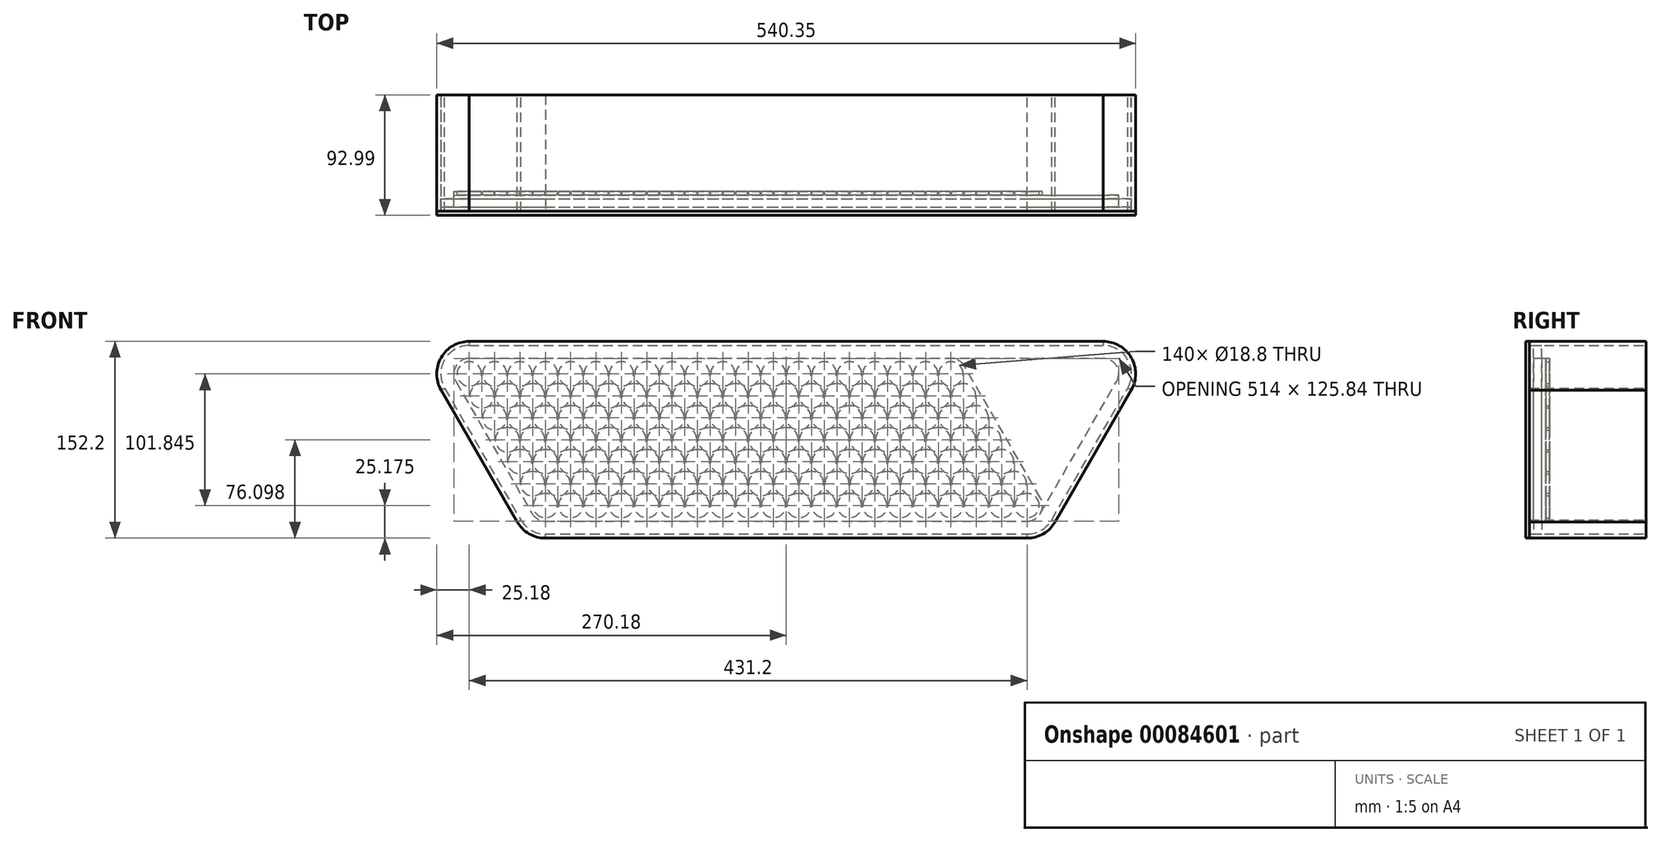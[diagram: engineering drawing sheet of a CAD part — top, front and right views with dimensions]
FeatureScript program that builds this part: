
annotation { "Feature Type Name" : "Feature", "Feature Type Description" : "" }
export const myFeature = defineFeature(function(context is Context, id is Id, definition is map)
    precondition{}
    {
        {
            var Q0;
            Q0=qCreatedBy(makeId("Front.planeOp"),FACE);
            var sketch = newSketch(context, id + "F0", { "sketchPlane" : qUnion([Q0]) });
            skLineSegment(sketch, "E0", {"start": v(0, 0) * mm, "end": v(79.44, 0) * mm, "construction": true});
            skLineSegment(sketch, "E1", {"start": v(0, 0) * mm, "end": v(43.4, -75.16) * mm, "construction": true});
            skCircle(sketch, "E2", {"center": v(0, 0) * mm, "radius": 9.4 * mm});
            skCircle(sketch, "E3.1.0.0", {"center": v(19.6, 0) * mm, "radius": 9.4 * mm});
            skCircle(sketch, "E3.2.0.0", {"center": v(39.2, 0) * mm, "radius": 9.4 * mm});
            skCircle(sketch, "E3.3.0.0", {"center": v(58.8, 0) * mm, "radius": 9.4 * mm});
            skCircle(sketch, "E3.4.0.0", {"center": v(78.4, 0) * mm, "radius": 9.4 * mm});
            skCircle(sketch, "E3.5.0.0", {"center": v(98, 0) * mm, "radius": 9.4 * mm});
            skCircle(sketch, "E3.6.0.0", {"center": v(117.6, 0) * mm, "radius": 9.4 * mm});
            skCircle(sketch, "E3.7.0.0", {"center": v(137.2, 0) * mm, "radius": 9.4 * mm});
            skCircle(sketch, "E3.8.0.0", {"center": v(156.8, 0) * mm, "radius": 9.4 * mm});
            skCircle(sketch, "E3.9.0.0", {"center": v(176.4, 0) * mm, "radius": 9.4 * mm});
            skCircle(sketch, "E3.10.0.0", {"center": v(196, 0) * mm, "radius": 9.4 * mm});
            skCircle(sketch, "E3.11.0.0", {"center": v(215.6, 0) * mm, "radius": 9.4 * mm});
            skCircle(sketch, "E3.12.0.0", {"center": v(235.2, 0) * mm, "radius": 9.4 * mm});
            skCircle(sketch, "E3.13.0.0", {"center": v(254.8, 0) * mm, "radius": 9.4 * mm});
            skCircle(sketch, "E3.14.0.0", {"center": v(274.4, 0) * mm, "radius": 9.4 * mm});
            skCircle(sketch, "E3.15.0.0", {"center": v(294, 0) * mm, "radius": 9.4 * mm});
            skCircle(sketch, "E3.16.0.0", {"center": v(313.6, 0) * mm, "radius": 9.4 * mm});
            skCircle(sketch, "E3.17.0.0", {"center": v(333.2, 0) * mm, "radius": 9.4 * mm});
            skCircle(sketch, "E3.18.0.0", {"center": v(352.8, 0) * mm, "radius": 9.4 * mm});
            skCircle(sketch, "E3.19.0.0", {"center": v(372.4, 0) * mm, "radius": 9.4 * mm});
            skLineSegment(sketch, "E3.direction1", {"start": v(0, 0) * mm, "end": v(19.6, 0) * mm, "construction": true});
            skCircle(sketch, "E4.1.0.0", {"center": v(9.8, -16.97) * mm, "radius": 9.4 * mm});
            skCircle(sketch, "E4.2.0.0", {"center": v(19.6, -33.95) * mm, "radius": 9.4 * mm});
            skCircle(sketch, "E4.3.0.0", {"center": v(29.4, -50.92) * mm, "radius": 9.4 * mm});
            skCircle(sketch, "E4.4.0.0", {"center": v(39.2, -67.9) * mm, "radius": 9.4 * mm});
            skCircle(sketch, "E4.5.0.0", {"center": v(49, -84.87) * mm, "radius": 9.4 * mm});
            skCircle(sketch, "E4.6.0.0", {"center": v(58.8, -101.84) * mm, "radius": 9.4 * mm});
            skLineSegment(sketch, "E4.direction1", {"start": v(0, 0) * mm, "end": v(9.8, -16.97) * mm, "construction": true});
            skCircle(sketch, "E5.1.0.0", {"center": v(29.4, -16.97) * mm, "radius": 9.4 * mm});
            skCircle(sketch, "E5.1.0.1", {"center": v(39.2, -33.95) * mm, "radius": 9.4 * mm});
            skCircle(sketch, "E5.1.0.2", {"center": v(49, -50.92) * mm, "radius": 9.4 * mm});
            skCircle(sketch, "E5.1.0.3", {"center": v(58.8, -67.9) * mm, "radius": 9.4 * mm});
            skCircle(sketch, "E5.1.0.4", {"center": v(68.6, -84.87) * mm, "radius": 9.4 * mm});
            skCircle(sketch, "E5.1.0.5", {"center": v(78.4, -101.84) * mm, "radius": 9.4 * mm});
            skCircle(sketch, "E5.2.0.0", {"center": v(49, -16.97) * mm, "radius": 9.4 * mm});
            skCircle(sketch, "E5.2.0.1", {"center": v(58.8, -33.95) * mm, "radius": 9.4 * mm});
            skCircle(sketch, "E5.2.0.2", {"center": v(68.6, -50.92) * mm, "radius": 9.4 * mm});
            skCircle(sketch, "E5.2.0.3", {"center": v(78.4, -67.9) * mm, "radius": 9.4 * mm});
            skCircle(sketch, "E5.2.0.4", {"center": v(88.2, -84.87) * mm, "radius": 9.4 * mm});
            skCircle(sketch, "E5.2.0.5", {"center": v(98, -101.84) * mm, "radius": 9.4 * mm});
            skCircle(sketch, "E5.3.0.0", {"center": v(68.6, -16.97) * mm, "radius": 9.4 * mm});
            skCircle(sketch, "E5.3.0.1", {"center": v(78.4, -33.95) * mm, "radius": 9.4 * mm});
            skCircle(sketch, "E5.3.0.2", {"center": v(88.2, -50.92) * mm, "radius": 9.4 * mm});
            skCircle(sketch, "E5.3.0.3", {"center": v(98, -67.9) * mm, "radius": 9.4 * mm});
            skCircle(sketch, "E5.3.0.4", {"center": v(107.8, -84.87) * mm, "radius": 9.4 * mm});
            skCircle(sketch, "E5.3.0.5", {"center": v(117.6, -101.84) * mm, "radius": 9.4 * mm});
            skCircle(sketch, "E5.4.0.0", {"center": v(88.2, -16.97) * mm, "radius": 9.4 * mm});
            skCircle(sketch, "E5.4.0.1", {"center": v(98, -33.95) * mm, "radius": 9.4 * mm});
            skCircle(sketch, "E5.4.0.2", {"center": v(107.8, -50.92) * mm, "radius": 9.4 * mm});
            skCircle(sketch, "E5.4.0.3", {"center": v(117.6, -67.9) * mm, "radius": 9.4 * mm});
            skCircle(sketch, "E5.4.0.4", {"center": v(127.4, -84.87) * mm, "radius": 9.4 * mm});
            skCircle(sketch, "E5.4.0.5", {"center": v(137.2, -101.84) * mm, "radius": 9.4 * mm});
            skCircle(sketch, "E5.5.0.0", {"center": v(107.8, -16.97) * mm, "radius": 9.4 * mm});
            skCircle(sketch, "E5.5.0.1", {"center": v(117.6, -33.95) * mm, "radius": 9.4 * mm});
            skCircle(sketch, "E5.5.0.2", {"center": v(127.4, -50.92) * mm, "radius": 9.4 * mm});
            skCircle(sketch, "E5.5.0.3", {"center": v(137.2, -67.9) * mm, "radius": 9.4 * mm});
            skCircle(sketch, "E5.5.0.4", {"center": v(147, -84.87) * mm, "radius": 9.4 * mm});
            skCircle(sketch, "E5.5.0.5", {"center": v(156.8, -101.84) * mm, "radius": 9.4 * mm});
            skCircle(sketch, "E5.6.0.0", {"center": v(127.4, -16.97) * mm, "radius": 9.4 * mm});
            skCircle(sketch, "E5.6.0.1", {"center": v(137.2, -33.95) * mm, "radius": 9.4 * mm});
            skCircle(sketch, "E5.6.0.2", {"center": v(147, -50.92) * mm, "radius": 9.4 * mm});
            skCircle(sketch, "E5.6.0.3", {"center": v(156.8, -67.9) * mm, "radius": 9.4 * mm});
            skCircle(sketch, "E5.6.0.4", {"center": v(166.6, -84.87) * mm, "radius": 9.4 * mm});
            skCircle(sketch, "E5.6.0.5", {"center": v(176.4, -101.84) * mm, "radius": 9.4 * mm});
            skCircle(sketch, "E5.7.0.0", {"center": v(147, -16.97) * mm, "radius": 9.4 * mm});
            skCircle(sketch, "E5.7.0.1", {"center": v(156.8, -33.95) * mm, "radius": 9.4 * mm});
            skCircle(sketch, "E5.7.0.2", {"center": v(166.6, -50.92) * mm, "radius": 9.4 * mm});
            skCircle(sketch, "E5.7.0.3", {"center": v(176.4, -67.9) * mm, "radius": 9.4 * mm});
            skCircle(sketch, "E5.7.0.4", {"center": v(186.2, -84.87) * mm, "radius": 9.4 * mm});
            skCircle(sketch, "E5.7.0.5", {"center": v(196, -101.84) * mm, "radius": 9.4 * mm});
            skCircle(sketch, "E5.8.0.0", {"center": v(166.6, -16.97) * mm, "radius": 9.4 * mm});
            skCircle(sketch, "E5.8.0.1", {"center": v(176.4, -33.95) * mm, "radius": 9.4 * mm});
            skCircle(sketch, "E5.8.0.2", {"center": v(186.2, -50.92) * mm, "radius": 9.4 * mm});
            skCircle(sketch, "E5.8.0.3", {"center": v(196, -67.9) * mm, "radius": 9.4 * mm});
            skCircle(sketch, "E5.8.0.4", {"center": v(205.8, -84.87) * mm, "radius": 9.4 * mm});
            skCircle(sketch, "E5.8.0.5", {"center": v(215.6, -101.84) * mm, "radius": 9.4 * mm});
            skCircle(sketch, "E5.9.0.0", {"center": v(186.2, -16.97) * mm, "radius": 9.4 * mm});
            skCircle(sketch, "E5.9.0.1", {"center": v(196, -33.95) * mm, "radius": 9.4 * mm});
            skCircle(sketch, "E5.9.0.2", {"center": v(205.8, -50.92) * mm, "radius": 9.4 * mm});
            skCircle(sketch, "E5.9.0.3", {"center": v(215.6, -67.9) * mm, "radius": 9.4 * mm});
            skCircle(sketch, "E5.9.0.4", {"center": v(225.4, -84.87) * mm, "radius": 9.4 * mm});
            skCircle(sketch, "E5.9.0.5", {"center": v(235.2, -101.84) * mm, "radius": 9.4 * mm});
            skCircle(sketch, "E5.10.0.0", {"center": v(205.8, -16.97) * mm, "radius": 9.4 * mm});
            skCircle(sketch, "E5.10.0.1", {"center": v(215.6, -33.95) * mm, "radius": 9.4 * mm});
            skCircle(sketch, "E5.10.0.2", {"center": v(225.4, -50.92) * mm, "radius": 9.4 * mm});
            skCircle(sketch, "E5.10.0.3", {"center": v(235.2, -67.9) * mm, "radius": 9.4 * mm});
            skCircle(sketch, "E5.10.0.4", {"center": v(245, -84.87) * mm, "radius": 9.4 * mm});
            skCircle(sketch, "E5.10.0.5", {"center": v(254.8, -101.84) * mm, "radius": 9.4 * mm});
            skCircle(sketch, "E5.11.0.0", {"center": v(225.4, -16.97) * mm, "radius": 9.4 * mm});
            skCircle(sketch, "E5.11.0.1", {"center": v(235.2, -33.95) * mm, "radius": 9.4 * mm});
            skCircle(sketch, "E5.11.0.2", {"center": v(245, -50.92) * mm, "radius": 9.4 * mm});
            skCircle(sketch, "E5.11.0.3", {"center": v(254.8, -67.9) * mm, "radius": 9.4 * mm});
            skCircle(sketch, "E5.11.0.4", {"center": v(264.6, -84.87) * mm, "radius": 9.4 * mm});
            skCircle(sketch, "E5.11.0.5", {"center": v(274.4, -101.84) * mm, "radius": 9.4 * mm});
            skCircle(sketch, "E5.12.0.0", {"center": v(245, -16.97) * mm, "radius": 9.4 * mm});
            skCircle(sketch, "E5.12.0.1", {"center": v(254.8, -33.95) * mm, "radius": 9.4 * mm});
            skCircle(sketch, "E5.12.0.2", {"center": v(264.6, -50.92) * mm, "radius": 9.4 * mm});
            skCircle(sketch, "E5.12.0.3", {"center": v(274.4, -67.9) * mm, "radius": 9.4 * mm});
            skCircle(sketch, "E5.12.0.4", {"center": v(284.2, -84.87) * mm, "radius": 9.4 * mm});
            skCircle(sketch, "E5.12.0.5", {"center": v(294, -101.84) * mm, "radius": 9.4 * mm});
            skCircle(sketch, "E5.13.0.0", {"center": v(264.6, -16.97) * mm, "radius": 9.4 * mm});
            skCircle(sketch, "E5.13.0.1", {"center": v(274.4, -33.95) * mm, "radius": 9.4 * mm});
            skCircle(sketch, "E5.13.0.2", {"center": v(284.2, -50.92) * mm, "radius": 9.4 * mm});
            skCircle(sketch, "E5.13.0.3", {"center": v(294, -67.9) * mm, "radius": 9.4 * mm});
            skCircle(sketch, "E5.13.0.4", {"center": v(303.8, -84.87) * mm, "radius": 9.4 * mm});
            skCircle(sketch, "E5.13.0.5", {"center": v(313.6, -101.84) * mm, "radius": 9.4 * mm});
            skCircle(sketch, "E5.14.0.0", {"center": v(284.2, -16.97) * mm, "radius": 9.4 * mm});
            skCircle(sketch, "E5.14.0.1", {"center": v(294, -33.95) * mm, "radius": 9.4 * mm});
            skCircle(sketch, "E5.14.0.2", {"center": v(303.8, -50.92) * mm, "radius": 9.4 * mm});
            skCircle(sketch, "E5.14.0.3", {"center": v(313.6, -67.9) * mm, "radius": 9.4 * mm});
            skCircle(sketch, "E5.14.0.4", {"center": v(323.4, -84.87) * mm, "radius": 9.4 * mm});
            skCircle(sketch, "E5.14.0.5", {"center": v(333.2, -101.84) * mm, "radius": 9.4 * mm});
            skCircle(sketch, "E5.15.0.0", {"center": v(303.8, -16.97) * mm, "radius": 9.4 * mm});
            skCircle(sketch, "E5.15.0.1", {"center": v(313.6, -33.95) * mm, "radius": 9.4 * mm});
            skCircle(sketch, "E5.15.0.2", {"center": v(323.4, -50.92) * mm, "radius": 9.4 * mm});
            skCircle(sketch, "E5.15.0.3", {"center": v(333.2, -67.9) * mm, "radius": 9.4 * mm});
            skCircle(sketch, "E5.15.0.4", {"center": v(343, -84.87) * mm, "radius": 9.4 * mm});
            skCircle(sketch, "E5.15.0.5", {"center": v(352.8, -101.84) * mm, "radius": 9.4 * mm});
            skCircle(sketch, "E5.16.0.0", {"center": v(323.4, -16.97) * mm, "radius": 9.4 * mm});
            skCircle(sketch, "E5.16.0.1", {"center": v(333.2, -33.95) * mm, "radius": 9.4 * mm});
            skCircle(sketch, "E5.16.0.2", {"center": v(343, -50.92) * mm, "radius": 9.4 * mm});
            skCircle(sketch, "E5.16.0.3", {"center": v(352.8, -67.9) * mm, "radius": 9.4 * mm});
            skCircle(sketch, "E5.16.0.4", {"center": v(362.6, -84.87) * mm, "radius": 9.4 * mm});
            skCircle(sketch, "E5.16.0.5", {"center": v(372.4, -101.84) * mm, "radius": 9.4 * mm});
            skCircle(sketch, "E5.17.0.0", {"center": v(343, -16.97) * mm, "radius": 9.4 * mm});
            skCircle(sketch, "E5.17.0.1", {"center": v(352.8, -33.95) * mm, "radius": 9.4 * mm});
            skCircle(sketch, "E5.17.0.2", {"center": v(362.6, -50.92) * mm, "radius": 9.4 * mm});
            skCircle(sketch, "E5.17.0.3", {"center": v(372.4, -67.9) * mm, "radius": 9.4 * mm});
            skCircle(sketch, "E5.17.0.4", {"center": v(382.2, -84.87) * mm, "radius": 9.4 * mm});
            skCircle(sketch, "E5.17.0.5", {"center": v(392, -101.84) * mm, "radius": 9.4 * mm});
            skCircle(sketch, "E5.18.0.0", {"center": v(362.6, -16.97) * mm, "radius": 9.4 * mm});
            skCircle(sketch, "E5.18.0.1", {"center": v(372.4, -33.95) * mm, "radius": 9.4 * mm});
            skCircle(sketch, "E5.18.0.2", {"center": v(382.2, -50.92) * mm, "radius": 9.4 * mm});
            skCircle(sketch, "E5.18.0.3", {"center": v(392, -67.9) * mm, "radius": 9.4 * mm});
            skCircle(sketch, "E5.18.0.4", {"center": v(401.8, -84.87) * mm, "radius": 9.4 * mm});
            skCircle(sketch, "E5.18.0.5", {"center": v(411.6, -101.84) * mm, "radius": 9.4 * mm});
            skCircle(sketch, "E5.19.0.0", {"center": v(382.2, -16.97) * mm, "radius": 9.4 * mm});
            skCircle(sketch, "E5.19.0.1", {"center": v(392, -33.95) * mm, "radius": 9.4 * mm});
            skCircle(sketch, "E5.19.0.2", {"center": v(401.8, -50.92) * mm, "radius": 9.4 * mm});
            skCircle(sketch, "E5.19.0.3", {"center": v(411.6, -67.9) * mm, "radius": 9.4 * mm});
            skCircle(sketch, "E5.19.0.4", {"center": v(421.4, -84.87) * mm, "radius": 9.4 * mm});
            skCircle(sketch, "E5.19.0.5", {"center": v(431.2, -101.84) * mm, "radius": 9.4 * mm});
            skLineSegment(sketch, "E5.direction1", {"start": v(9.8, -16.97) * mm, "end": v(29.4, -16.97) * mm, "construction": true});
            skLineSegment(sketch, "E6", {"start": v(0, 0) * mm, "end": v(372.4, 0) * mm, "construction": true});
            skLineSegment(sketch, "E7", {"start": v(372.4, 0) * mm, "end": v(441, -118.82) * mm, "construction": true});
            skLineSegment(sketch, "E8", {"start": v(441, -118.82) * mm, "end": v(68.6, -118.82) * mm, "construction": true});
            skLineSegment(sketch, "E9", {"start": v(68.6, -118.82) * mm, "end": v(0, 0) * mm, "construction": true});
            skArc(sketch, "E10", {"start": v(48.4, -107.84) * mm, "mid": v(52.8, -112.24) * mm, "end": v(58.8, -113.84) * mm});
            skArc(sketch, "E11", {"start": v(431.2, -113.84) * mm, "mid": v(441.6, -107.84) * mm, "end": v(441.6, -95.84) * mm});
            skArc(sketch, "E12", {"start": v(382.8, 6) * mm, "mid": v(378.4, 10.4) * mm, "end": v(372.4, 12) * mm});
            skArc(sketch, "E13", {"start": v(0, 12) * mm, "mid": v(-10.4, 6) * mm, "end": v(-10.4, -6) * mm});
            skLineSegment(sketch, "E14", {"start": v(0, 12) * mm, "end": v(372.4, 12) * mm});
            skLineSegment(sketch, "E15", {"start": v(-10.4, -6) * mm, "end": v(48.4, -107.84) * mm});
            skLineSegment(sketch, "E16", {"start": v(58.8, -113.84) * mm, "end": v(431.2, -113.84) * mm});
            skLineSegment(sketch, "E17", {"start": v(441.6, -95.84) * mm, "end": v(382.8, 6) * mm});
            skLineSegment(sketch, "E18", {"start": v(441.6, -107.84) * mm, "end": v(500.4, -6) * mm, "construction": true});
            skLineSegment(sketch, "E19", {"start": v(372.4, 12) * mm, "end": v(490, 12) * mm, "construction": true});
            skPoint(sketch, "E20.visualSharp", {"position": v(510.78, 12) * mm});
            skArc(sketch, "E20.filletArc", {"start": v(500.4, -6) * mm, "mid": v(500.4, 6) * mm, "end": v(490, 12) * mm, "construction": true});
            skSolve(sketch);
        }
        {
            var Q0;
            Q0=makeQuery(id+"F0.imprint","IMPRINT",FACE,{"disambiguationData":[TD([[makeQuery(id+"F0.imprint","IMPRINT",EDGE,{"derivedFrom":sQuery(id+"F0.wireOp",EDGE,"E2")}),-1.0]])]});
            extrude(context, id + "F1", {"entities" : qUnion([Q0]), "depth" : 3 * mm});
        }
        {
            var Q0;
            Q0=makeQuery(id+"F1.opExtrude","CAP_FACE",FACE,{"disambiguationData":[OSD([sQuery(id+"F0.wireOp",EDGE,"E2"),sQuery(id+"F0.wireOp",EDGE,"E3.1.0.0"),sQuery(id+"F0.wireOp",EDGE,"E3.2.0.0"),sQuery(id+"F0.wireOp",EDGE,"E3.3.0.0"),sQuery(id+"F0.wireOp",EDGE,"E3.4.0.0"),sQuery(id+"F0.wireOp",EDGE,"E3.5.0.0"),sQuery(id+"F0.wireOp",EDGE,"E3.6.0.0"),sQuery(id+"F0.wireOp",EDGE,"E3.7.0.0"),sQuery(id+"F0.wireOp",EDGE,"E3.8.0.0"),sQuery(id+"F0.wireOp",EDGE,"E3.9.0.0"),sQuery(id+"F0.wireOp",EDGE,"E3.10.0.0"),sQuery(id+"F0.wireOp",EDGE,"E3.11.0.0"),sQuery(id+"F0.wireOp",EDGE,"E3.12.0.0"),sQuery(id+"F0.wireOp",EDGE,"E3.13.0.0"),sQuery(id+"F0.wireOp",EDGE,"E3.14.0.0"),sQuery(id+"F0.wireOp",EDGE,"E3.15.0.0"),sQuery(id+"F0.wireOp",EDGE,"E3.16.0.0"),sQuery(id+"F0.wireOp",EDGE,"E3.17.0.0"),sQuery(id+"F0.wireOp",EDGE,"E3.18.0.0"),sQuery(id+"F0.wireOp",EDGE,"E3.19.0.0"),sQuery(id+"F0.wireOp",EDGE,"E4.1.0.0"),sQuery(id+"F0.wireOp",EDGE,"E4.2.0.0"),sQuery(id+"F0.wireOp",EDGE,"E4.3.0.0"),sQuery(id+"F0.wireOp",EDGE,"E4.4.0.0"),sQuery(id+"F0.wireOp",EDGE,"E4.5.0.0"),sQuery(id+"F0.wireOp",EDGE,"E4.6.0.0"),sQuery(id+"F0.wireOp",EDGE,"E5.1.0.0"),sQuery(id+"F0.wireOp",EDGE,"E5.1.0.1"),sQuery(id+"F0.wireOp",EDGE,"E5.1.0.2"),sQuery(id+"F0.wireOp",EDGE,"E5.1.0.3"),sQuery(id+"F0.wireOp",EDGE,"E5.1.0.4"),sQuery(id+"F0.wireOp",EDGE,"E5.1.0.5"),sQuery(id+"F0.wireOp",EDGE,"E5.2.0.0"),sQuery(id+"F0.wireOp",EDGE,"E5.2.0.1"),sQuery(id+"F0.wireOp",EDGE,"E5.2.0.2"),sQuery(id+"F0.wireOp",EDGE,"E5.2.0.3"),sQuery(id+"F0.wireOp",EDGE,"E5.2.0.4"),sQuery(id+"F0.wireOp",EDGE,"E5.2.0.5"),sQuery(id+"F0.wireOp",EDGE,"E5.3.0.0"),sQuery(id+"F0.wireOp",EDGE,"E5.3.0.1"),sQuery(id+"F0.wireOp",EDGE,"E5.3.0.2"),sQuery(id+"F0.wireOp",EDGE,"E5.3.0.3"),sQuery(id+"F0.wireOp",EDGE,"E5.3.0.4"),sQuery(id+"F0.wireOp",EDGE,"E5.3.0.5"),sQuery(id+"F0.wireOp",EDGE,"E5.4.0.0"),sQuery(id+"F0.wireOp",EDGE,"E5.4.0.1"),sQuery(id+"F0.wireOp",EDGE,"E5.4.0.2"),sQuery(id+"F0.wireOp",EDGE,"E5.4.0.3"),sQuery(id+"F0.wireOp",EDGE,"E5.4.0.4"),sQuery(id+"F0.wireOp",EDGE,"E5.4.0.5"),sQuery(id+"F0.wireOp",EDGE,"E5.5.0.0"),sQuery(id+"F0.wireOp",EDGE,"E5.5.0.1"),sQuery(id+"F0.wireOp",EDGE,"E5.5.0.2"),sQuery(id+"F0.wireOp",EDGE,"E5.5.0.3"),sQuery(id+"F0.wireOp",EDGE,"E5.5.0.4"),sQuery(id+"F0.wireOp",EDGE,"E5.5.0.5"),sQuery(id+"F0.wireOp",EDGE,"E5.6.0.0"),sQuery(id+"F0.wireOp",EDGE,"E5.6.0.1"),sQuery(id+"F0.wireOp",EDGE,"E5.6.0.2"),sQuery(id+"F0.wireOp",EDGE,"E5.6.0.3"),sQuery(id+"F0.wireOp",EDGE,"E5.6.0.4"),sQuery(id+"F0.wireOp",EDGE,"E5.6.0.5"),sQuery(id+"F0.wireOp",EDGE,"E5.7.0.0"),sQuery(id+"F0.wireOp",EDGE,"E5.7.0.1"),sQuery(id+"F0.wireOp",EDGE,"E5.7.0.2"),sQuery(id+"F0.wireOp",EDGE,"E5.7.0.3"),sQuery(id+"F0.wireOp",EDGE,"E5.7.0.4"),sQuery(id+"F0.wireOp",EDGE,"E5.7.0.5"),sQuery(id+"F0.wireOp",EDGE,"E5.8.0.0"),sQuery(id+"F0.wireOp",EDGE,"E5.8.0.1"),sQuery(id+"F0.wireOp",EDGE,"E5.8.0.2"),sQuery(id+"F0.wireOp",EDGE,"E5.8.0.3"),sQuery(id+"F0.wireOp",EDGE,"E5.8.0.4"),sQuery(id+"F0.wireOp",EDGE,"E5.8.0.5"),sQuery(id+"F0.wireOp",EDGE,"E5.9.0.0"),sQuery(id+"F0.wireOp",EDGE,"E5.9.0.1"),sQuery(id+"F0.wireOp",EDGE,"E5.9.0.2"),sQuery(id+"F0.wireOp",EDGE,"E5.9.0.3"),sQuery(id+"F0.wireOp",EDGE,"E5.9.0.4"),sQuery(id+"F0.wireOp",EDGE,"E5.9.0.5"),sQuery(id+"F0.wireOp",EDGE,"E5.10.0.0"),sQuery(id+"F0.wireOp",EDGE,"E5.10.0.1"),sQuery(id+"F0.wireOp",EDGE,"E5.10.0.2"),sQuery(id+"F0.wireOp",EDGE,"E5.10.0.3"),sQuery(id+"F0.wireOp",EDGE,"E5.10.0.4"),sQuery(id+"F0.wireOp",EDGE,"E5.10.0.5"),sQuery(id+"F0.wireOp",EDGE,"E5.11.0.0"),sQuery(id+"F0.wireOp",EDGE,"E5.11.0.1"),sQuery(id+"F0.wireOp",EDGE,"E5.11.0.2"),sQuery(id+"F0.wireOp",EDGE,"E5.11.0.3"),sQuery(id+"F0.wireOp",EDGE,"E5.11.0.4"),sQuery(id+"F0.wireOp",EDGE,"E5.11.0.5"),sQuery(id+"F0.wireOp",EDGE,"E5.12.0.0"),sQuery(id+"F0.wireOp",EDGE,"E5.12.0.1"),sQuery(id+"F0.wireOp",EDGE,"E5.12.0.2"),sQuery(id+"F0.wireOp",EDGE,"E5.12.0.3"),sQuery(id+"F0.wireOp",EDGE,"E5.12.0.4"),sQuery(id+"F0.wireOp",EDGE,"E5.12.0.5"),sQuery(id+"F0.wireOp",EDGE,"E5.13.0.0"),sQuery(id+"F0.wireOp",EDGE,"E5.13.0.1"),sQuery(id+"F0.wireOp",EDGE,"E5.13.0.2"),sQuery(id+"F0.wireOp",EDGE,"E5.13.0.3"),sQuery(id+"F0.wireOp",EDGE,"E5.13.0.4"),sQuery(id+"F0.wireOp",EDGE,"E5.13.0.5"),sQuery(id+"F0.wireOp",EDGE,"E5.14.0.0"),sQuery(id+"F0.wireOp",EDGE,"E5.14.0.1"),sQuery(id+"F0.wireOp",EDGE,"E5.14.0.2"),sQuery(id+"F0.wireOp",EDGE,"E5.14.0.3"),sQuery(id+"F0.wireOp",EDGE,"E5.14.0.4"),sQuery(id+"F0.wireOp",EDGE,"E5.14.0.5"),sQuery(id+"F0.wireOp",EDGE,"E5.15.0.0"),sQuery(id+"F0.wireOp",EDGE,"E5.15.0.1"),sQuery(id+"F0.wireOp",EDGE,"E5.15.0.2"),sQuery(id+"F0.wireOp",EDGE,"E5.15.0.3"),sQuery(id+"F0.wireOp",EDGE,"E5.15.0.4"),sQuery(id+"F0.wireOp",EDGE,"E5.15.0.5"),sQuery(id+"F0.wireOp",EDGE,"E5.16.0.0"),sQuery(id+"F0.wireOp",EDGE,"E5.16.0.1"),sQuery(id+"F0.wireOp",EDGE,"E5.16.0.2"),sQuery(id+"F0.wireOp",EDGE,"E5.16.0.3"),sQuery(id+"F0.wireOp",EDGE,"E5.16.0.4"),sQuery(id+"F0.wireOp",EDGE,"E5.16.0.5"),sQuery(id+"F0.wireOp",EDGE,"E5.17.0.0"),sQuery(id+"F0.wireOp",EDGE,"E5.17.0.1"),sQuery(id+"F0.wireOp",EDGE,"E5.17.0.2"),sQuery(id+"F0.wireOp",EDGE,"E5.17.0.3"),sQuery(id+"F0.wireOp",EDGE,"E5.17.0.4"),sQuery(id+"F0.wireOp",EDGE,"E5.17.0.5"),sQuery(id+"F0.wireOp",EDGE,"E5.18.0.0"),sQuery(id+"F0.wireOp",EDGE,"E5.18.0.1"),sQuery(id+"F0.wireOp",EDGE,"E5.18.0.2"),sQuery(id+"F0.wireOp",EDGE,"E5.18.0.3"),sQuery(id+"F0.wireOp",EDGE,"E5.18.0.4"),sQuery(id+"F0.wireOp",EDGE,"E5.18.0.5"),sQuery(id+"F0.wireOp",EDGE,"E5.19.0.0"),sQuery(id+"F0.wireOp",EDGE,"E5.19.0.1"),sQuery(id+"F0.wireOp",EDGE,"E5.19.0.2"),sQuery(id+"F0.wireOp",EDGE,"E5.19.0.3"),sQuery(id+"F0.wireOp",EDGE,"E5.19.0.4"),sQuery(id+"F0.wireOp",EDGE,"E5.19.0.5"),sQuery(id+"F0.wireOp",EDGE,"E10"),sQuery(id+"F0.wireOp",EDGE,"E11"),sQuery(id+"F0.wireOp",EDGE,"E13"),sQuery(id+"F0.wireOp",EDGE,"E14"),sQuery(id+"F0.wireOp",EDGE,"E15"),sQuery(id+"F0.wireOp",EDGE,"E16"),sQuery(id+"F0.wireOp",EDGE,"E18"),sQuery(id+"F0.wireOp",EDGE,"E19"),sQuery(id+"F0.wireOp",EDGE,"E20.filletArc")])],"isStart":false});
            var sketch = newSketch(context, id + "F2", { "sketchPlane" : qUnion([Q0]) });
            skLineSegment(sketch, "E21.0", {"start": v(0, 12) * mm, "end": v(490, 12) * mm});
            skArc(sketch, "E21.1", {"start": v(0, 12) * mm, "mid": v(-10.4, 6) * mm, "end": v(-10.4, -6) * mm});
            skLineSegment(sketch, "E21.2", {"start": v(-10.4, -6) * mm, "end": v(48.4, -107.84) * mm});
            skArc(sketch, "E21.3", {"start": v(48.4, -107.84) * mm, "mid": v(52.8, -112.24) * mm, "end": v(58.8, -113.84) * mm});
            skLineSegment(sketch, "E21.4", {"start": v(58.8, -113.84) * mm, "end": v(431.2, -113.84) * mm});
            skLineSegment(sketch, "E21.5", {"start": v(431.2, -113.84) * mm, "end": v(431.2, -113.84) * mm});
            skLineSegment(sketch, "E22", {"start": v(441.6, -107.84) * mm, "end": v(500.4, -6) * mm});
            skArc(sketch, "E23", {"start": v(431.2, -113.84) * mm, "mid": v(437.2, -112.24) * mm, "end": v(441.6, -107.84) * mm});
            skPoint(sketch, "E24.orphan", {"position": v(562.43, 12) * mm});
            skPoint(sketch, "E25.visualSharp", {"position": v(510.78, 12) * mm});
            skArc(sketch, "E25.filletArc", {"start": v(500.4, -6) * mm, "mid": v(500.4, 6) * mm, "end": v(490, 12) * mm});
            skSolve(sketch);
        }
        {
            var Q0;
            Q0 = qSketchRegion(id + "F2", true);
            extrude(context, id + "F3", {"entities" : qUnion([Q0]), "depth" : 3 * mm});
        }
        {
            var Q0;
            Q0=makeQuery(id+"F3.opExtrude","CAP_FACE",FACE,{"disambiguationData":[OSD([sQuery(id+"F2.wireOp",EDGE,"E21.0"),sQuery(id+"F2.wireOp",EDGE,"E21.1"),sQuery(id+"F2.wireOp",EDGE,"E21.2"),sQuery(id+"F2.wireOp",EDGE,"E21.3"),sQuery(id+"F2.wireOp",EDGE,"E21.4"),sQuery(id+"F2.wireOp",EDGE,"E22"),sQuery(id+"F2.wireOp",EDGE,"E23"),sQuery(id+"F2.wireOp",EDGE,"E25.filletArc")])],"isStart":false});
            var sketch = newSketch(context, id + "F4", { "sketchPlane" : qUnion([Q0]) });
            skLineSegment(sketch, "E26.0", {"start": v(0, 12) * mm, "end": v(490, 12) * mm});
            skArc(sketch, "E27.0", {"start": v(0, 12) * mm, "mid": v(-10.4, 6) * mm, "end": v(-10.4, -6) * mm});
            skLineSegment(sketch, "E28.0", {"start": v(-10.4, -6) * mm, "end": v(48.4, -107.84) * mm});
            skArc(sketch, "E29.0", {"start": v(48.4, -107.84) * mm, "mid": v(52.8, -112.24) * mm, "end": v(58.8, -113.84) * mm});
            skLineSegment(sketch, "E30.0", {"start": v(58.8, -113.84) * mm, "end": v(431.2, -113.84) * mm});
            skArc(sketch, "E31.0", {"start": v(500.4, -6) * mm, "mid": v(500.4, 6) * mm, "end": v(490, 12) * mm});
            skLineSegment(sketch, "E32.0", {"start": v(441.6, -107.84) * mm, "end": v(500.4, -6) * mm});
            skArc(sketch, "E33.0", {"start": v(431.2, -113.84) * mm, "mid": v(437.2, -112.24) * mm, "end": v(441.6, -107.84) * mm});
            skArc(sketch, "E34.0", {"start": v(0, 22) * mm, "mid": v(-19.05, 11) * mm, "end": v(-19.05, -11) * mm});
            skLineSegment(sketch, "E34.1", {"start": v(-19.05, -11) * mm, "end": v(39.75, -112.84) * mm});
            skLineSegment(sketch, "E34.2", {"start": v(0, 22) * mm, "end": v(490, 22) * mm});
            skArc(sketch, "E34.3", {"start": v(39.75, -112.84) * mm, "mid": v(47.8, -120.9) * mm, "end": v(58.8, -123.84) * mm});
            skArc(sketch, "E34.4", {"start": v(509.05, -11) * mm, "mid": v(509.05, 11) * mm, "end": v(490, 22) * mm});
            skLineSegment(sketch, "E34.5", {"start": v(450.25, -112.84) * mm, "end": v(509.05, -11) * mm});
            skArc(sketch, "E34.6", {"start": v(431.2, -123.84) * mm, "mid": v(442.2, -120.9) * mm, "end": v(450.25, -112.84) * mm});
            skLineSegment(sketch, "E34.7", {"start": v(58.8, -123.84) * mm, "end": v(431.2, -123.84) * mm});
            skSolve(sketch);
        }
        {
            var Q0;
            Q0 = qSketchRegion(id + "F4", true);
            extrude(context, id + "F5", {"entities" : qUnion([Q0]), "depth" : 6.35 * mm});
        }
        {
            var Q0;
            Q0=makeQuery(id+"F5.opExtrude","CAP_FACE",FACE,{"disambiguationData":[OSD([sQuery(id+"F4.wireOp",EDGE,"E26.0"),sQuery(id+"F4.wireOp",EDGE,"E27.0"),sQuery(id+"F4.wireOp",EDGE,"E28.0"),sQuery(id+"F4.wireOp",EDGE,"E29.0"),sQuery(id+"F4.wireOp",EDGE,"E30.0"),sQuery(id+"F4.wireOp",EDGE,"E31.0"),sQuery(id+"F4.wireOp",EDGE,"E32.0"),sQuery(id+"F4.wireOp",EDGE,"E33.0"),sQuery(id+"F4.wireOp",EDGE,"E34.0"),sQuery(id+"F4.wireOp",EDGE,"E34.1"),sQuery(id+"F4.wireOp",EDGE,"E34.2"),sQuery(id+"F4.wireOp",EDGE,"E34.3"),sQuery(id+"F4.wireOp",EDGE,"E34.4"),sQuery(id+"F4.wireOp",EDGE,"E34.5"),sQuery(id+"F4.wireOp",EDGE,"E34.6"),sQuery(id+"F4.wireOp",EDGE,"E34.7")])],"isStart":false});
            var sketch = newSketch(context, id + "F6", { "sketchPlane" : qUnion([Q0]) });
            skLineSegment(sketch, "E35.0", {"start": v(0, 22) * mm, "end": v(490, 22) * mm});
            skArc(sketch, "E35.1", {"start": v(0, 22) * mm, "mid": v(-19.05, 11) * mm, "end": v(-19.05, -11) * mm});
            skLineSegment(sketch, "E35.2", {"start": v(-19.05, -11) * mm, "end": v(39.75, -112.84) * mm});
            skArc(sketch, "E35.3", {"start": v(39.75, -112.84) * mm, "mid": v(47.8, -120.9) * mm, "end": v(58.8, -123.84) * mm});
            skLineSegment(sketch, "E35.4", {"start": v(58.8, -123.84) * mm, "end": v(431.2, -123.84) * mm});
            skArc(sketch, "E35.5", {"start": v(431.2, -123.84) * mm, "mid": v(442.2, -120.9) * mm, "end": v(450.25, -112.84) * mm});
            skLineSegment(sketch, "E35.6", {"start": v(450.25, -112.84) * mm, "end": v(509.05, -11) * mm});
            skArc(sketch, "E35.7", {"start": v(509.05, -11) * mm, "mid": v(509.05, 11) * mm, "end": v(490, 22) * mm});
            skSolve(sketch);
        }
        {
            var Q0;
            Q0 = qSketchRegion(id + "F6", true);
            extrude(context, id + "F7", {"entities" : qUnion([Q0]), "depth" : 3.17 * mm});
        }
        {
            var Q0;
            Q0=makeQuery(id+"F5.opExtrude","CAP_FACE",FACE,{"disambiguationData":[OSD([sQuery(id+"F4.wireOp",EDGE,"E26.0"),sQuery(id+"F4.wireOp",EDGE,"E27.0"),sQuery(id+"F4.wireOp",EDGE,"E28.0"),sQuery(id+"F4.wireOp",EDGE,"E29.0"),sQuery(id+"F4.wireOp",EDGE,"E30.0"),sQuery(id+"F4.wireOp",EDGE,"E31.0"),sQuery(id+"F4.wireOp",EDGE,"E32.0"),sQuery(id+"F4.wireOp",EDGE,"E33.0"),sQuery(id+"F4.wireOp",EDGE,"E34.0"),sQuery(id+"F4.wireOp",EDGE,"E34.1"),sQuery(id+"F4.wireOp",EDGE,"E34.2"),sQuery(id+"F4.wireOp",EDGE,"E34.3"),sQuery(id+"F4.wireOp",EDGE,"E34.4"),sQuery(id+"F4.wireOp",EDGE,"E34.5"),sQuery(id+"F4.wireOp",EDGE,"E34.6"),sQuery(id+"F4.wireOp",EDGE,"E34.7")])],"isStart":true});
            var sketch = newSketch(context, id + "F8", { "sketchPlane" : qUnion([Q0]) });
            skLineSegment(sketch, "E36.0", {"start": v(0, 22) * mm, "end": v(-490, 22) * mm});
            skLineSegment(sketch, "E37.0", {"start": v(0, 18.82) * mm, "end": v(-490, 18.83) * mm});
            skLineSegment(sketch, "E38", {"start": v(-490, 18.83) * mm, "end": v(-490, 22) * mm});
            skLineSegment(sketch, "E39", {"start": v(0, 22) * mm, "end": v(0, 18.82) * mm});
            skSolve(sketch);
        }
        {
            var Q0;
            Q0 = qSketchRegion(id + "F8", true);
            extrude(context, id + "F9", {"entities" : qUnion([Q0]), "depth" : 85 * mm});
        }
        {
            var Q0;
            Q0=makeQuery(id+"F9.opExtrude","SWEPT_BODY",BODY,{"disambiguationData":[OSD([sQuery(id+"F8.wireOp",EDGE,"E36.0"),sQuery(id+"F8.wireOp",EDGE,"E37.0"),sQuery(id+"F8.wireOp",EDGE,"E38"),sQuery(id+"F8.wireOp",EDGE,"E39")])]});
            deleteBodies(context, id + "F10", {"entities" : qUnion([Q0])});
        }
        {
            var Q0;
            Q0=makeQuery(id+"F7.opExtrude","SWEPT_FACE",FACE,{"disambiguationData":[OSD([sQuery(id+"F6.wireOp",EDGE,"E35.0")])]});
            var sketch = newSketch(context, id + "F11", { "sketchPlane" : qUnion([Q0]) });
            skLineSegment(sketch, "E40.0", {"start": v(0, -15.53) * mm, "end": v(490, -15.53) * mm});
            skLineSegment(sketch, "E41.0", {"start": v(0, 74.47) * mm, "end": v(490, 74.47) * mm});
            skLineSegment(sketch, "E42", {"start": v(490, -15.52) * mm, "end": v(490, 74.47) * mm});
            skLineSegment(sketch, "E43", {"start": v(0, -15.52) * mm, "end": v(0, 74.47) * mm});
            skSolve(sketch);
        }
        {
            var Q0;
            Q0 = qSketchRegion(id + "F11", true);
            extrude(context, id + "F12", {"entities" : qUnion([Q0]), "depth" : 3.17 * mm});
        }
        {
            var Q0;
            Q0=makeQuery(id+"F7.opExtrude","SWEPT_FACE",FACE,{"disambiguationData":[OSD([sQuery(id+"F6.wireOp",EDGE,"E35.6")])]});
            var sketch = newSketch(context, id + "F13", { "sketchPlane" : qUnion([Q0]) });
            skLineSegment(sketch, "E44.0", {"start": v(-15.53, 127.4) * mm, "end": v(-15.53, 245) * mm});
            skLineSegment(sketch, "E45.0", {"start": v(74.47, 127.4) * mm, "end": v(74.47, 245) * mm});
            skLineSegment(sketch, "E46", {"start": v(-15.52, 245) * mm, "end": v(74.47, 245) * mm});
            skLineSegment(sketch, "E47", {"start": v(-15.52, 127.4) * mm, "end": v(74.47, 127.4) * mm});
            skSolve(sketch);
        }
        {
            var Q0;
            Q0 = qSketchRegion(id + "F13", true);
            extrude(context, id + "F14", {"entities" : qUnion([Q0]), "depth" : 3.17 * mm});
        }
        {
            var Q0;
            Q0=makeQuery(id+"F5.opExtrude","SWEPT_FACE",FACE,{"disambiguationData":[OSD([sQuery(id+"F4.wireOp",EDGE,"E34.7")])]});
            var sketch = newSketch(context, id + "F15", { "sketchPlane" : qUnion([Q0]) });
            skLineSegment(sketch, "E48.0", {"start": v(58.8, 15.53) * mm, "end": v(431.2, 15.53) * mm});
            skLineSegment(sketch, "E49.0", {"start": v(58.8, -74.47) * mm, "end": v(431.2, -74.47) * mm});
            skLineSegment(sketch, "E50", {"start": v(431.2, 15.53) * mm, "end": v(431.2, -74.47) * mm});
            skLineSegment(sketch, "E51", {"start": v(58.8, -74.47) * mm, "end": v(58.8, 15.53) * mm});
            skSolve(sketch);
        }
        {
            var Q0;
            Q0 = qSketchRegion(id + "F15", true);
            extrude(context, id + "F16", {"entities" : qUnion([Q0]), "depth" : 3.17 * mm});
        }
        {
            var Q0;
            Q0=makeQuery(id+"F12.opExtrude","SWEPT_FACE",FACE,{"disambiguationData":[OSD([sQuery(id+"F11.wireOp",EDGE,"E42")])]});
            var sketch = newSketch(context, id + "F17", { "sketchPlane" : qUnion([Q0]) });
            skLineSegment(sketch, "E52.0", {"start": v(-15.53, 25.18) * mm, "end": v(74.47, 25.18) * mm});
            skLineSegment(sketch, "E52.1", {"start": v(74.47, 25.18) * mm, "end": v(74.47, 22) * mm});
            skLineSegment(sketch, "E52.2", {"start": v(-15.53, 22) * mm, "end": v(74.47, 22) * mm});
            skLineSegment(sketch, "E52.3", {"start": v(-15.53, 25.18) * mm, "end": v(-15.53, 22) * mm});
            skSolve(sketch);
        }
        {
            var Q0;
            Q0=makeQuery(id+"F17.imprint","IMPRINT",FACE,{"disambiguationData":[TD([[makeQuery(id+"F17.imprint","IMPRINT",EDGE,{"derivedFrom":sQuery(id+"F17.wireOp",EDGE,"E52.0")}),-1.0]])]});
            var Q1;
            Q1=makeQuery(id+"F7.opExtrude","CAP_EDGE",EDGE,{"disambiguationData":[OSD([sQuery(id+"F6.wireOp",EDGE,"E35.7")])],"isStart":false});
            sweep(context, id + "F18", {"profiles" : qUnion([Q0]), "path" : qUnion([Q1])});
        }
        {
            var Q0;
            Q0=makeQuery(id+"F14.opExtrude","SWEPT_FACE",FACE,{"disambiguationData":[OSD([sQuery(id+"F13.wireOp",EDGE,"E47")])]});
            var sketch = newSketch(context, id + "F19", { "sketchPlane" : qUnion([Q0]) });
            skLineSegment(sketch, "E53.0.0", {"start": v(446.35, 15.53) * mm, "end": v(446.35, -74.47) * mm});
            skLineSegment(sketch, "E53.0.1", {"start": v(446.35, -74.47) * mm, "end": v(449.53, -74.47) * mm});
            skLineSegment(sketch, "E53.0.2", {"start": v(449.53, -74.47) * mm, "end": v(449.53, 15.53) * mm});
            skLineSegment(sketch, "E53.0.3", {"start": v(449.53, 15.53) * mm, "end": v(446.35, 15.53) * mm});
            skSolve(sketch);
        }
        {
            var Q0;
            Q0=makeQuery(id+"F19.imprint","IMPRINT",FACE,{"disambiguationData":[TD([[makeQuery(id+"F19.imprint","IMPRINT",EDGE,{"derivedFrom":sQuery(id+"F19.wireOp",EDGE,"E53.0.0")}),1.0]])]});
            var Q1;
            Q1=makeQuery(id+"F7.opExtrude","CAP_EDGE",EDGE,{"disambiguationData":[OSD([sQuery(id+"F6.wireOp",EDGE,"E35.5")])],"isStart":false});
            sweep(context, id + "F20", {"profiles" : qUnion([Q0]), "path" : qUnion([Q1])});
        }
        {
            var Q0;
            Q0=makeQuery(id+"F7.opExtrude","SWEPT_FACE",FACE,{"disambiguationData":[OSD([sQuery(id+"F6.wireOp",EDGE,"E35.2")])]});
            var sketch = newSketch(context, id + "F21", { "sketchPlane" : qUnion([Q0]) });
            skLineSegment(sketch, "E54.0", {"start": v(15.53, 0) * mm, "end": v(15.53, -117.6) * mm});
            skLineSegment(sketch, "E55.0", {"start": v(-74.47, 0) * mm, "end": v(-74.47, -117.6) * mm});
            skLineSegment(sketch, "E56", {"start": v(15.52, 0) * mm, "end": v(-74.47, 0) * mm});
            skLineSegment(sketch, "E57", {"start": v(15.52, -117.6) * mm, "end": v(-74.47, -117.6) * mm});
            skSolve(sketch);
        }
        {
            var Q0;
            Q0 = qSketchRegion(id + "F21", true);
            extrude(context, id + "F22", {"entities" : qUnion([Q0]), "depth" : 3.17 * mm});
        }
        {
            var Q0;
            Q0=makeQuery(id+"F12.opExtrude","SWEPT_FACE",FACE,{"disambiguationData":[OSD([sQuery(id+"F11.wireOp",EDGE,"E43")])]});
            var Q1;
            Q1=makeQuery(id+"F7.opExtrude","CAP_EDGE",EDGE,{"disambiguationData":[OSD([sQuery(id+"F6.wireOp",EDGE,"E35.1")])],"isStart":false});
            sweep(context, id + "F23", {"profiles" : qUnion([Q0]), "path" : qUnion([Q1])});
        }
        {
            var Q0;
            Q0=makeQuery(id+"F22.opExtrude","SWEPT_FACE",FACE,{"disambiguationData":[OSD([sQuery(id+"F21.wireOp",EDGE,"E57")])]});
            var Q1;
            Q1=makeQuery(id+"F7.opExtrude","CAP_EDGE",EDGE,{"disambiguationData":[OSD([sQuery(id+"F6.wireOp",EDGE,"E35.3")])],"isStart":false});
            sweep(context, id + "F24", {"profiles" : qUnion([Q0]), "path" : qUnion([Q1])});
        }
        {
            var Q0;
            Q0=makeQuery(id+"F7.opExtrude","CAP_FACE",FACE,{"disambiguationData":[OSD([sQuery(id+"F6.wireOp",EDGE,"E35.0"),sQuery(id+"F6.wireOp",EDGE,"E35.1"),sQuery(id+"F6.wireOp",EDGE,"E35.2"),sQuery(id+"F6.wireOp",EDGE,"E35.3"),sQuery(id+"F6.wireOp",EDGE,"E35.4"),sQuery(id+"F6.wireOp",EDGE,"E35.5"),sQuery(id+"F6.wireOp",EDGE,"E35.6"),sQuery(id+"F6.wireOp",EDGE,"E35.7")])],"isStart":false});
            var sketch = newSketch(context, id + "F25", { "sketchPlane" : qUnion([Q0]) });
            skLineSegment(sketch, "E58.0", {"start": v(0, 25.18) * mm, "end": v(490, 25.18) * mm});
            skArc(sketch, "E58.1", {"start": v(0, 25.18) * mm, "mid": v(-21.8, 12.59) * mm, "end": v(-21.8, -12.59) * mm});
            skLineSegment(sketch, "E58.2", {"start": v(-21.8, -12.59) * mm, "end": v(37, -114.43) * mm});
            skArc(sketch, "E58.3", {"start": v(37, -114.43) * mm, "mid": v(46.21, -123.65) * mm, "end": v(58.8, -127.02) * mm});
            skLineSegment(sketch, "E58.4", {"start": v(58.8, -127.02) * mm, "end": v(431.2, -127.02) * mm});
            skArc(sketch, "E58.5", {"start": v(453, -114.43) * mm, "mid": v(443.79, -123.65) * mm, "end": v(431.2, -127.02) * mm});
            skLineSegment(sketch, "E58.6", {"start": v(453, -114.43) * mm, "end": v(511.8, -12.59) * mm});
            skArc(sketch, "E58.7", {"start": v(490, 25.18) * mm, "mid": v(511.8, 12.59) * mm, "end": v(511.8, -12.59) * mm});
            skSolve(sketch);
        }
        {
            var Q0;
            Q0 = qSketchRegion(id + "F25", true);
            extrude(context, id + "F26", {"entities" : qUnion([Q0]), "depth" : 3 * mm});
        }
    });
